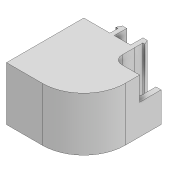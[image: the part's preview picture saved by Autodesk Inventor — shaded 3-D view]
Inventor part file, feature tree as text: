
AUTODESK INVENTOR PART (.ipt)
format: ipt  version: 2021 (Build 250183000, 183)  size: 187,904 bytes
history: native  units: mm
features: other x5, plane x2, extrude x2, sketch x2
ambient origin geometry x8: Origin, YZ Plane, XZ Plane, XY Plane, X Axis, Y Axis, Z Axis, Center Point
bodies: Volumenkörper1 (feature_tree)
feature tree (11):
  other  "Corner_Layout.ipt"
  plane  "Arbeitsebene1"
  other  "Trennen1"
  plane  "Arbeitsebene2"
  other  "Trennen2"
  extrude  "Extrusion1"  [1 undecoded]
  extrude  "Extrusion2"  TaperAngle=0.0deg  [1 undecoded]
  other  "Volumenkörper1::Corner_Layout.ipt"
  other  "Bezeichnung1"
  sketch  "Skizze1"  dims[d0=10.0mm d1=-16.0mm]
  sketch  "Skizze2"  dims[d2=3.5mm d3=0.0mm d4=0.0mm d5=0.0mm d6=0.0mm]
note: 2 required parameter values undecoded (feature->parameter linkage not recoverable at this tier; creation-order binding heuristic only, values carry confidence <= 0.55)
